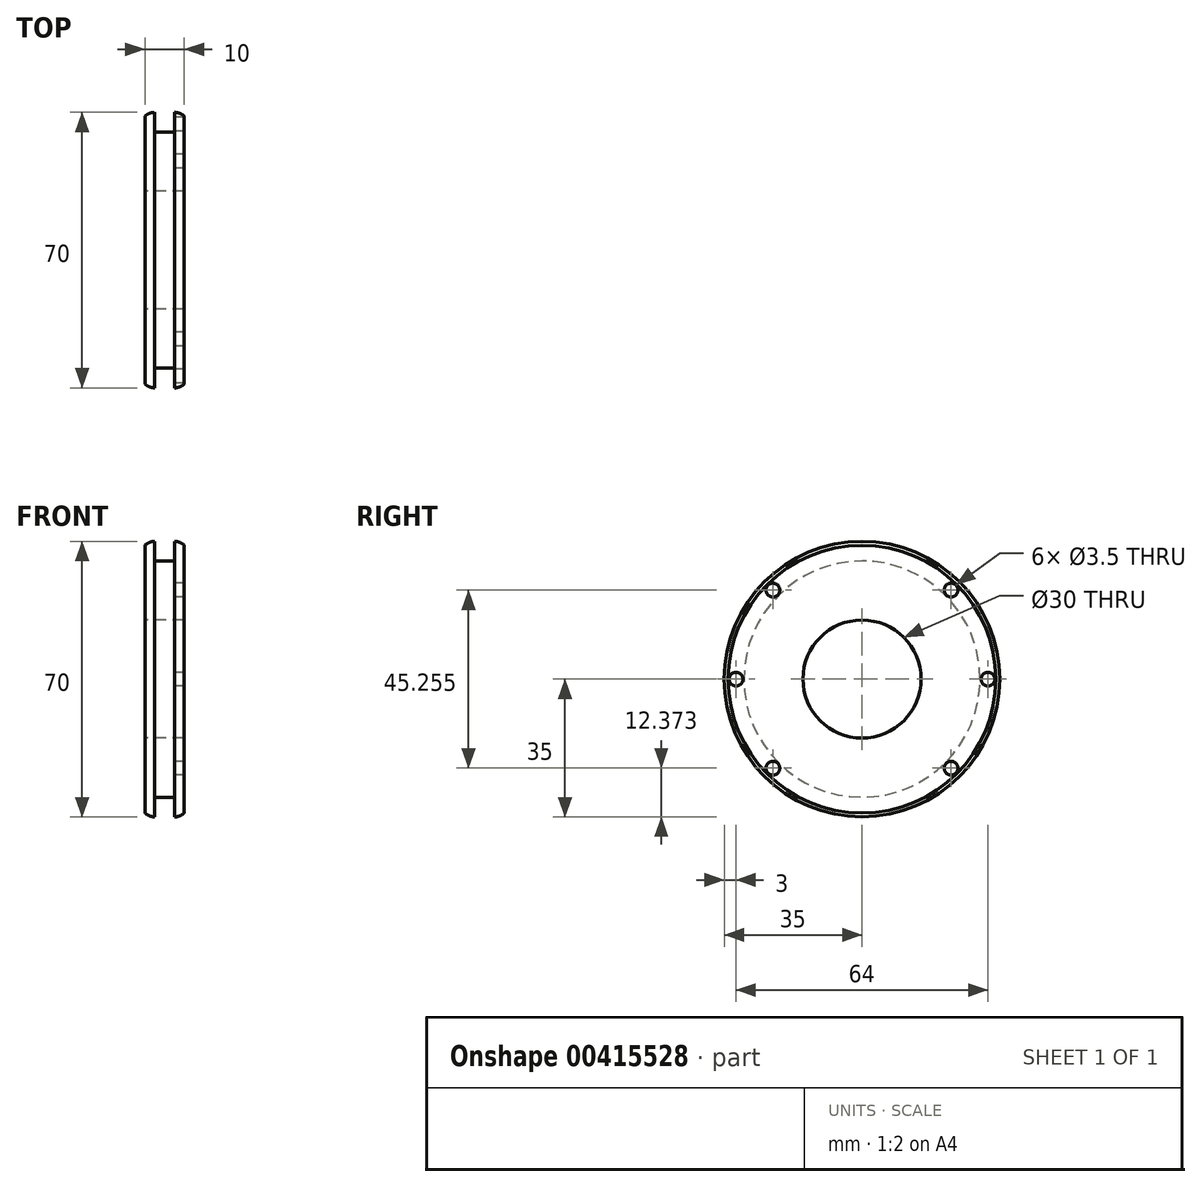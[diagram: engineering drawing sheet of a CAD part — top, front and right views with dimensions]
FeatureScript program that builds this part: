
annotation { "Feature Type Name" : "Feature", "Feature Type Description" : "" }
export const myFeature = defineFeature(function(context is Context, id is Id, definition is map)
    precondition{}
    {
        {
            var Q0;
            Q0=qCreatedBy(makeId("Front.planeOp"),FACE);
            var sketch = newSketch(context, id + "F0", { "sketchPlane" : qUnion([Q0])});
            skLineSegment(sketch, "E0", {"start": v(0, 0) * mm, "end": v(0, 30) * mm});
            skLineSegment(sketch, "E1", {"start": v(0, 30) * mm, "end": v(2.5, 30) * mm});
            skLineSegment(sketch, "E2", {"start": v(0, 30) * mm, "end": v(-2.5, 30) * mm});
            skLineSegment(sketch, "E3", {"start": v(-5, 30) * mm, "end": v(-5, 20) * mm});
            skLineSegment(sketch, "E4", {"start": v(5, 20) * mm, "end": v(5, 30) * mm});
            skLineSegment(sketch, "E5", {"start": v(5, 20) * mm, "end": v(5, 15) * mm});
            skLineSegment(sketch, "E6", {"start": v(5, 15) * mm, "end": v(0, 15) * mm});
            skLineSegment(sketch, "E7", {"start": v(0, 15) * mm, "end": v(-5, 15) * mm});
            skLineSegment(sketch, "E8", {"start": v(-5, 15) * mm, "end": v(-5, 20) * mm});
            skLineSegment(sketch, "E9", {"start": v(2.5, 30) * mm, "end": v(2.5, 35) * mm});
            skLineSegment(sketch, "E10", {"start": v(-2.5, 35) * mm, "end": v(-2.5, 30) * mm});
            skLineSegment(sketch, "E11", {"start": v(-5, 30) * mm, "end": v(-5, 34) * mm});
            skLineSegment(sketch, "E12", {"start": v(5, 30) * mm, "end": v(5, 34) * mm});
            skArc(sketch, "E13", {"start": v(2.5, 35) * mm, "mid": v(3.85, 34.74) * mm, "end": v(5, 34) * mm});
            skArc(sketch, "E14", {"start": v(-2.5, 35) * mm, "mid": v(-3.85, 34.74) * mm, "end": v(-5, 34) * mm});
            skSolve(sketch);
        }
        {
            var Q0;
            Q0=qCreatedBy(makeId("Right.planeOp"),FACE);
            var sketch = newSketch(context, id + "F1", { "sketchPlane" : qUnion([Q0])});
            skCircle(sketch, "E15", {"center": v(0, 0) * mm, "radius": 30 * mm});
            skCircle(sketch, "E16.0", {"center": v(0, 0) * mm, "radius": 32 * mm});
            skCircle(sketch, "E17.1.0", {"center": v(22.63, 22.63) * mm, "radius": 1.75 * mm});
            skCircle(sketch, "E17.2.0", {"center": v(32, 0) * mm, "radius": 1.75 * mm});
            skLineSegment(sketch, "E17.anchor1", {"start": v(0, 0) * mm, "end": v(0, 32) * mm, "construction": true});
            skLineSegment(sketch, "E17.anchor2", {"start": v(0, 0) * mm, "end": v(32, 0) * mm, "construction": true});
            skCircle(sketch, "E18.1.0", {"center": v(22.63, -22.63) * mm, "radius": 1.75 * mm});
            skLineSegment(sketch, "E18.anchor2", {"start": v(0, 0) * mm, "end": v(0, -32) * mm, "construction": true});
            skCircle(sketch, "E19.1.0", {"center": v(-22.63, -22.63) * mm, "radius": 1.75 * mm});
            skCircle(sketch, "E19.2.0", {"center": v(-32, 0) * mm, "radius": 1.75 * mm});
            skLineSegment(sketch, "E19.anchor2", {"start": v(0, 0) * mm, "end": v(-32, 0) * mm, "construction": true});
            skCircle(sketch, "E20.1.0", {"center": v(-22.63, 22.63) * mm, "radius": 1.75 * mm});
            skSolve(sketch);
        }
        {
            var Q0;
            {var subQ0=sQuery(id+"F0.wireOp",EDGE,"E2");Q0=makeQuery(id+"F0.imprint","IMPRINT",FACE,{"disambiguationData":[TD([[makeQuery(id+"F0.imprint","IMPRINT",EDGE,{"derivedFrom":subQ0}),1.0]])]});}
            var Q1;
            {var subQ1=sQuery(id+"F0.wireOp",EDGE,"E1");Q1=makeQuery(id+"F0.imprint","IMPRINT",FACE,{"disambiguationData":[TD([[makeQuery(id+"F0.imprint","IMPRINT",EDGE,{"derivedFrom":subQ1}),-1.0]])]});}
            var Q2;
            Q2=sQuery(id+"F1.wireOp",EDGE,"E15");
            revolve(context, id + "F2", {"entities" : qUnion([Q0, Q1]), "axis" : qUnion([Q2]), "revolveType" : RevolveType.FULL});
        }
        {
            var Q0;
            Q0=sQuery(id+"F1.wireOp",VERTEX,"E20.1.0.center");
            var Q1;
            Q1=sQuery(id+"F1.wireOp",VERTEX,"E17.1.0.center");
            var Q2;
            Q2=sQuery(id+"F1.wireOp",VERTEX,"E17.anchor2.end");
            var Q3;
            Q3=sQuery(id+"F1.wireOp",VERTEX,"E18.1.0.center");
            var Q4;
            Q4=sQuery(id+"F1.wireOp",VERTEX,"E19.1.0.center");
            var Q5;
            Q5=sQuery(id+"F1.wireOp",VERTEX,"E19.anchor2.end");
            var Q6;
            Q6=makeQuery(id+"F2.opRevolve","SWEPT_BODY",BODY,{"disambiguationData":[OSD([sQuery(id+"F0.wireOp",EDGE,"E1"),sQuery(id+"F0.wireOp",EDGE,"E2"),sQuery(id+"F0.wireOp",EDGE,"E3"),sQuery(id+"F0.wireOp",EDGE,"E4"),sQuery(id+"F0.wireOp",EDGE,"E5"),sQuery(id+"F0.wireOp",EDGE,"E6"),sQuery(id+"F0.wireOp",EDGE,"E7"),sQuery(id+"F0.wireOp",EDGE,"E8"),sQuery(id+"F0.wireOp",EDGE,"E9"),sQuery(id+"F0.wireOp",EDGE,"E10"),sQuery(id+"F0.wireOp",EDGE,"E11"),sQuery(id+"F0.wireOp",EDGE,"E12"),sQuery(id+"F0.wireOp",EDGE,"E13"),sQuery(id+"F0.wireOp",EDGE,"E14")])]});
            hole(context, id + "F3", {"style" : HoleStyle.SIMPLE, "endStyle" : HoleEndStyle.BLIND, "oppositeDirection" : true, "holeDiameter" : 3.5 * mm, "holeDepth" : 12 * mm, "isTappedThrough" : true, "tappedDepth" : 12 * mm, "tapClearance" : 3, "locations" : qUnion([Q0, Q1, Q2, Q3, Q4, Q5]), "scope" : qUnion([Q6])});
        }
    });
